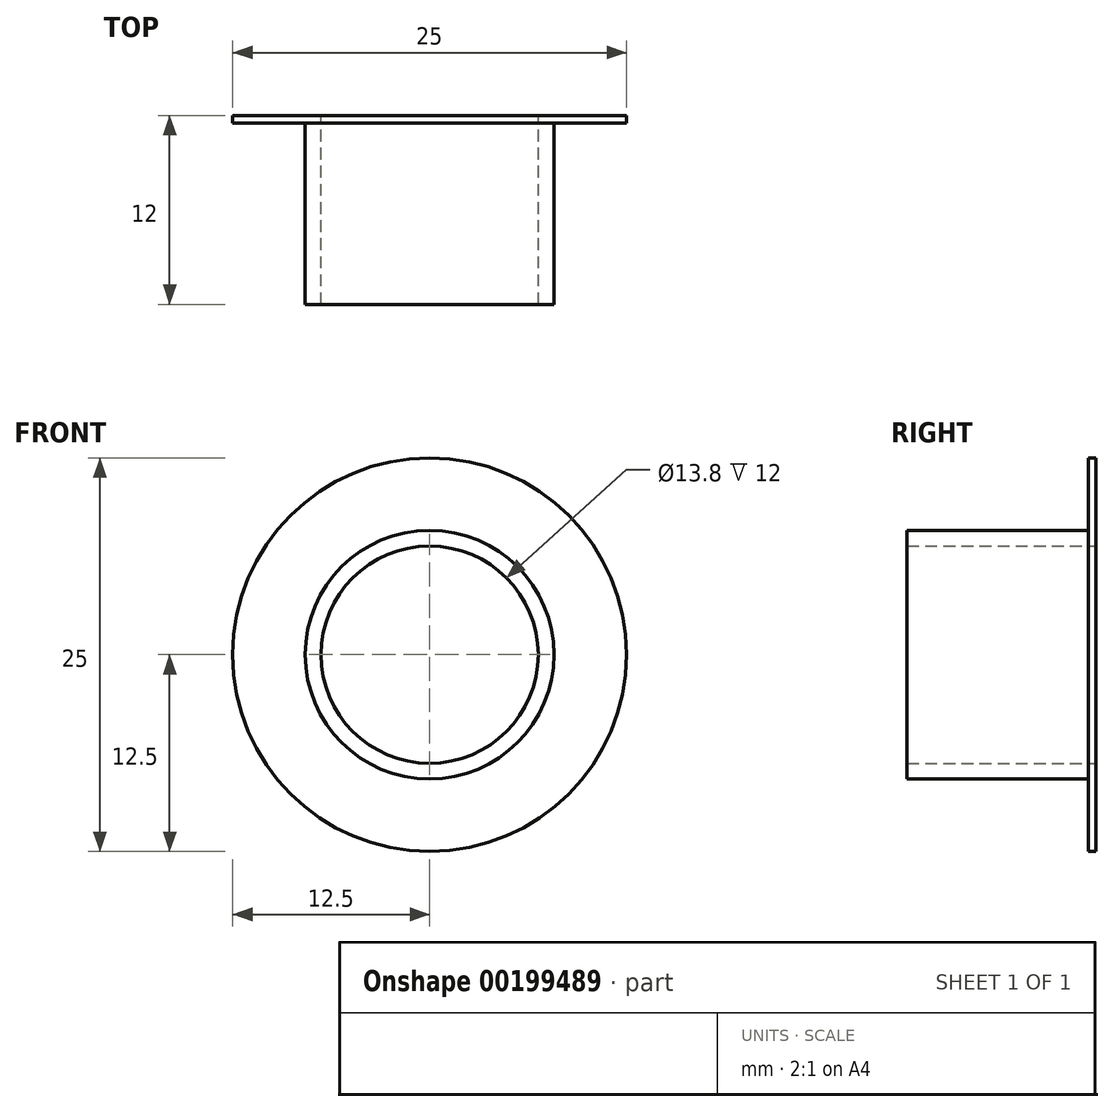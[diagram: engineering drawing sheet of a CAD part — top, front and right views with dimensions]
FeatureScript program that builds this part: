
annotation { "Feature Type Name" : "Feature", "Feature Type Description" : "" }
export const myFeature = defineFeature(function(context is Context, id is Id, definition is map)
    precondition{}
    {
        {
            var Q0;
            Q0=qCreatedBy(makeId("Front.planeOp"),FACE);
            var sketch = newSketch(context, id + "F0", { "sketchPlane" : qUnion([Q0])});
            skCircle(sketch, "E0", {"center": v(0, 0) * mm, "radius": 12.5 * mm});
            skCircle(sketch, "E1", {"center": v(0, 0) * mm, "radius": 6.9 * mm});
            skCircle(sketch, "E2", {"center": v(0, 0) * mm, "radius": 7.9 * mm});
            skSolve(sketch);
        }
        {
            var Q0;
            Q0=makeQuery(id+"F0.imprint","IMPRINT",FACE,{"disambiguationData":[TD([[makeQuery(id+"F0.imprint","IMPRINT",EDGE,{"derivedFrom":sQuery(id+"F0.wireOp",EDGE,"E1")}),-1.0]])]});
            extrude(context, id + "F1", {"entities" : qUnion([Q0]), "depth" : 12 * mm});
        }
        {
            var Q0;
            Q0=qCreatedBy(makeId("Front.planeOp"),FACE);
            var sketch = newSketch(context, id + "F2", { "sketchPlane" : qUnion([Q0])});
            skCircle(sketch, "E3", {"center": v(0, 0) * mm, "radius": 12.5 * mm});
            skSolve(sketch);
        }
        {
            var Q0;
            Q0=makeQuery(id+"F2.imprint","IMPRINT",FACE,{"disambiguationData":[TD([[makeQuery(id+"F2.imprint","IMPRINT",EDGE,{"derivedFrom":sQuery(id+"F2.wireOp",EDGE,"E3")}),1.0]])]});
            extrude(context, id + "F3", {"entities" : qUnion([Q0]), "operationType" : NewBodyOperationType.ADD, "depth" : 0.5 * mm});
        }
        {
            var Q0;
            Q0=makeQuery(id+"F3.boolean.opBoolean","SPLIT",FACE,{"disambiguationData":[TD([makeQuery(id+"F1.opExtrude","SWEPT_FACE",FACE,{"disambiguationData":[OSD([sQuery(id+"F0.wireOp",EDGE,"E1")])]})])],"derivedFrom":makeQuery(id+"F3.opExtrude","CAP_FACE",FACE,{"disambiguationData":[OSD([sQuery(id+"F2.wireOp",EDGE,"E3")])],"isStart":false})});
            extrude(context, id + "F4", {"entities" : qUnion([Q0]), "operationType" : NewBodyOperationType.REMOVE, "oppositeDirection" : true, "depth" : 0.5 * mm});
        }
    });
